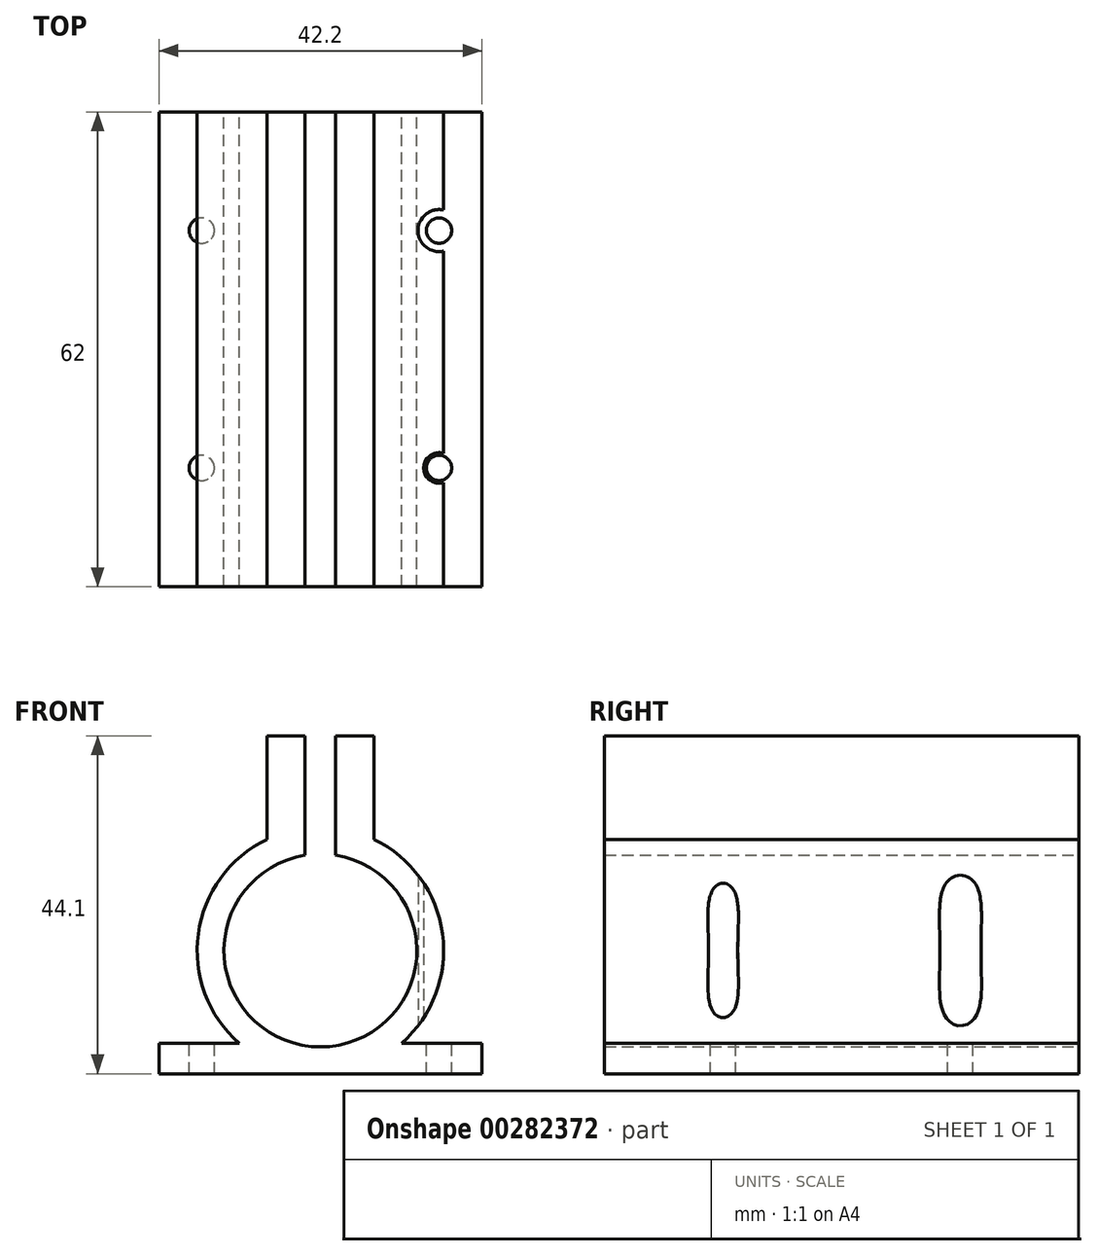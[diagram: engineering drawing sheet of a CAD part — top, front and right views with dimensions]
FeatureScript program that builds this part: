
annotation { "Feature Type Name" : "Feature", "Feature Type Description" : "" }
export const myFeature = defineFeature(function(context is Context, id is Id, definition is map)
    precondition{}
    {
        {
            var Q0;
            Q0=qCreatedBy(makeId("Front.planeOp"),FACE);
            var sketch = newSketch(context, id + "F0", { "sketchPlane" : qUnion([Q0])});
            skArc(sketch, "E0", {"start": v(-2, 12.44) * mm, "mid": v(0, -12.6) * mm, "end": v(2, 12.44) * mm});
            skArc(sketch, "E1", {"start": v(10.62, -12.1) * mm, "mid": v(15.95, 2.17) * mm, "end": v(7, 14.5) * mm});
            skLineSegment(sketch, "E2", {"start": v(0, 0) * mm, "end": v(0, -16.1) * mm, "construction": true});
            skLineSegment(sketch, "E3", {"start": v(0, -16.1) * mm, "end": v(21.1, -16.1) * mm});
            skLineSegment(sketch, "E4", {"start": v(21.1, -16.1) * mm, "end": v(21.1, -12.1) * mm});
            skLineSegment(sketch, "E5", {"start": v(21.1, -12.1) * mm, "end": v(10.62, -12.1) * mm});
            skLineSegment(sketch, "E6", {"start": v(-21.1, -12.1) * mm, "end": v(-21.1, -16.1) * mm});
            skLineSegment(sketch, "E7", {"start": v(-21.1, -16.1) * mm, "end": v(0, -16.1) * mm});
            skLineSegment(sketch, "E8.trimOffspring", {"start": v(-10.62, -12.1) * mm, "end": v(-21.1, -12.1) * mm});
            skLineSegment(sketch, "E9", {"start": v(0, 0) * mm, "end": v(0, 28) * mm, "construction": true});
            skLineSegment(sketch, "E10.0", {"start": v(2, 12.44) * mm, "end": v(2, 28) * mm});
            skLineSegment(sketch, "E11.0", {"start": v(-2, 12.44) * mm, "end": v(-2, 28) * mm});
            skLineSegment(sketch, "E12.0", {"start": v(7, 14.5) * mm, "end": v(7, 28) * mm});
            skLineSegment(sketch, "E13.0", {"start": v(-7, 14.5) * mm, "end": v(-7, 28) * mm});
            skLineSegment(sketch, "E14", {"start": v(-7, 28) * mm, "end": v(-2, 28) * mm});
            skLineSegment(sketch, "E15", {"start": v(2, 28) * mm, "end": v(7, 28) * mm});
            skArc(sketch, "E16.trimOffspring", {"start": v(-7, 14.5) * mm, "mid": v(-15.95, 2.17) * mm, "end": v(-10.62, -12.1) * mm});
            skSolve(sketch);
        }
        {
            var Q0;
            Q0=qSketchRegion(id+"F0",true);
            extrude(context, id + "F1", {"entities" : qUnion([Q0]), "depth" : 62 * mm});
        }
        {
            var Q0;
            Q0=makeQuery(id+"F1.opExtrude","SWEPT_FACE",FACE,{"disambiguationData":[OSD([sQuery(id+"F0.wireOp",EDGE,"E8.trimOffspring")])]});
            var sketch = newSketch(context, id + "F2", { "sketchPlane" : qUnion([Q0])});
            skLineSegment(sketch, "E17", {"start": v(-21.1, -31) * mm, "end": v(21.1, -31) * mm, "construction": true});
            skPoint(sketch, "E17.endSnap0", {"position": v(-10.62, -31) * mm});
            skLineSegment(sketch, "E18.bottom", {"start": v(15.5, -46.5) * mm, "end": v(-15.5, -46.5) * mm, "construction": true});
            skLineSegment(sketch, "E18.top", {"start": v(15.5, -15.5) * mm, "end": v(-15.5, -15.5) * mm, "construction": true});
            skLineSegment(sketch, "E18.left", {"start": v(15.5, -46.5) * mm, "end": v(15.5, -15.5) * mm, "construction": true});
            skLineSegment(sketch, "E18.right", {"start": v(-15.5, -46.5) * mm, "end": v(-15.5, -15.5) * mm, "construction": true});
            skPoint(sketch, "E18.middle", {"position": v(0, -31) * mm});
            skCircle(sketch, "E19", {"center": v(15.5, -15.5) * mm, "radius": 1.65 * mm});
            skCircle(sketch, "E20", {"center": v(15.5, -46.5) * mm, "radius": 1.65 * mm});
            skCircle(sketch, "E21", {"center": v(-15.5, -15.5) * mm, "radius": 1.65 * mm});
            skCircle(sketch, "E22", {"center": v(-15.5, -46.5) * mm, "radius": 1.65 * mm});
            skSolve(sketch);
        }
        {
            var Q0;
            Q0=qSketchRegion(id+"F2",true);
            extrude(context, id + "F3", {"entities" : qUnion([Q0]), "operationType" : NewBodyOperationType.REMOVE, "oppositeDirection" : true, "depth" : 25 * mm});
        }
        {
            var Q0;
            Q0=makeQuery(id+"F1.opExtrude","SWEPT_FACE",FACE,{"disambiguationData":[OSD([sQuery(id+"F0.wireOp",EDGE,"E5")])]});
            var sketch = newSketch(context, id + "F4", { "sketchPlane" : qUnion([Q0])});
            skCircle(sketch, "E23", {"center": v(15.5, -46.5) * mm, "radius": 2 * mm});
            skCircle(sketch, "E24", {"center": v(15.5, -15.5) * mm, "radius": 2.75 * mm});
            skSolve(sketch);
        }
        {
            var Q0;
            Q0=qSketchRegion(id+"F4",true);
            extrude(context, id + "F5", {"entities" : qUnion([Q0]), "operationType" : NewBodyOperationType.REMOVE, "depth" : 25 * mm});
        }
    });
